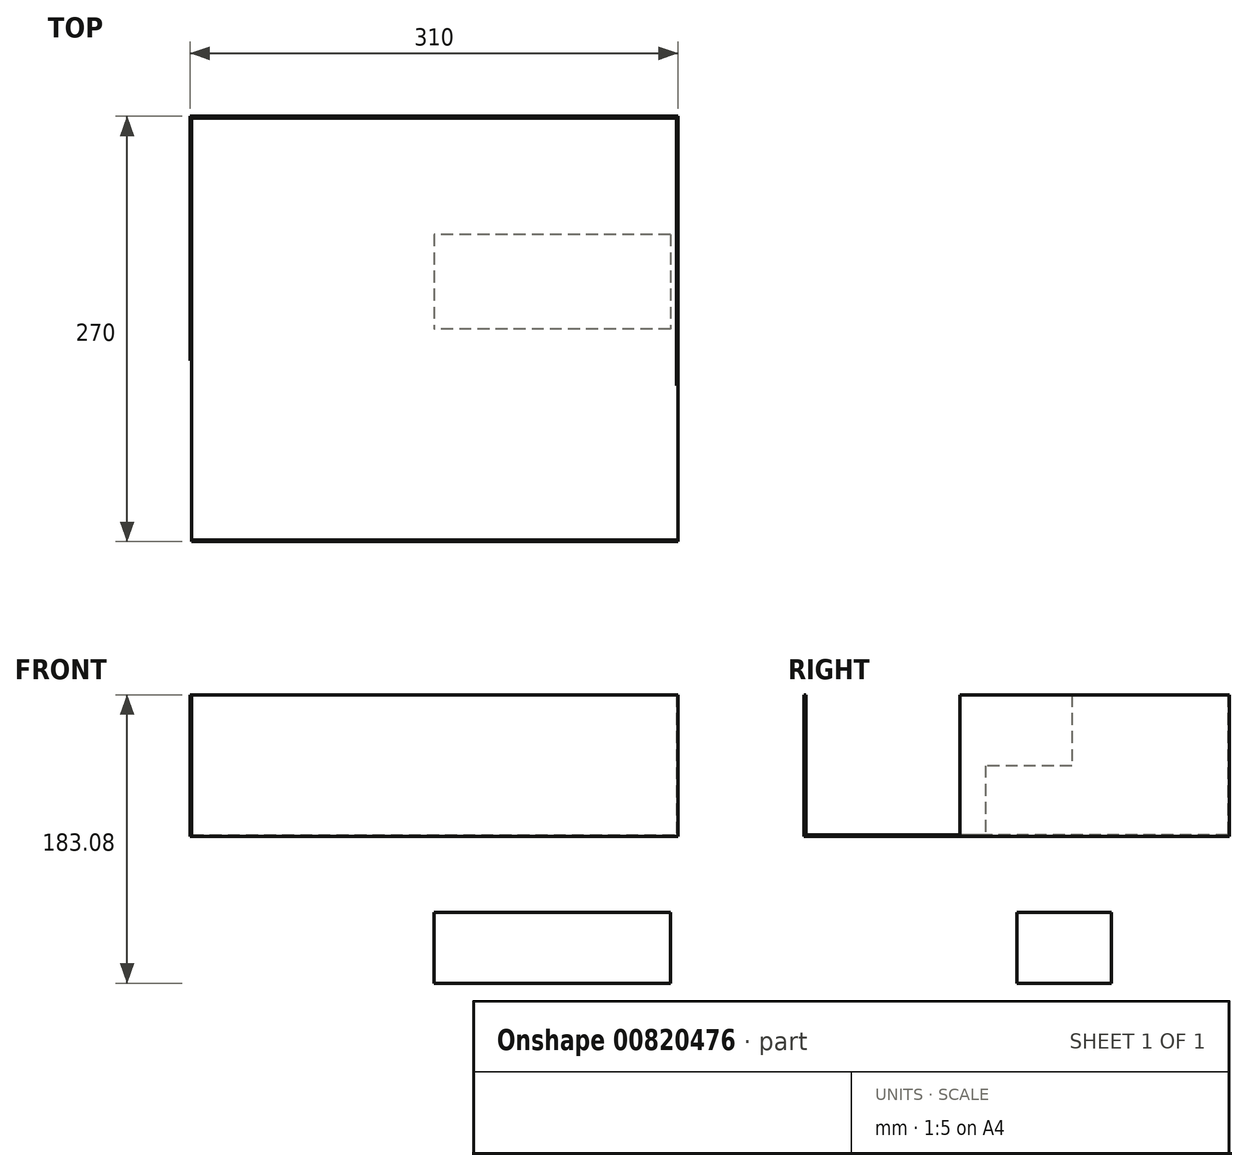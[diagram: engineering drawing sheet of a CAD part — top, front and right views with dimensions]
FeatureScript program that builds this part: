
annotation { "Feature Type Name" : "Feature", "Feature Type Description" : "" }
export const myFeature = defineFeature(function(context is Context, id is Id, definition is map)
    precondition{}
    {
        {
            var Q0;
            Q0=qCreatedBy(makeId("Top.planeOp"),FACE);
            var sketch = newSketch(context, id + "F0", { "sketchPlane" : qUnion([Q0])});
            skLineSegment(sketch, "E0.bottom", {"start": v(155, -135) * mm, "end": v(-155, -135) * mm});
            skLineSegment(sketch, "E0.top", {"start": v(155, 135) * mm, "end": v(-155, 135) * mm});
            skLineSegment(sketch, "E0.left", {"start": v(155, -135) * mm, "end": v(155, 135) * mm});
            skLineSegment(sketch, "E0.right", {"start": v(-155, -135) * mm, "end": v(-155, 135) * mm});
            skPoint(sketch, "E0.middle", {"position": v(0, 0) * mm});
            skLineSegment(sketch, "E1", {"start": v(-155, 135) * mm, "end": v(-155, 134) * mm});
            skLineSegment(sketch, "E2", {"start": v(-155, 134) * mm, "end": v(155, 134) * mm});
            skLineSegment(sketch, "E3", {"start": v(155, 134) * mm, "end": v(154, 134) * mm});
            skLineSegment(sketch, "E4", {"start": v(154, 134) * mm, "end": v(154, -36) * mm});
            skLineSegment(sketch, "E5", {"start": v(154, -36) * mm, "end": v(155, -36) * mm});
            skLineSegment(sketch, "E6", {"start": v(-155, 134) * mm, "end": v(-154, 134) * mm});
            skLineSegment(sketch, "E7", {"start": v(-154, 134) * mm, "end": v(-154, -135) * mm});
            skLineSegment(sketch, "E8", {"start": v(-154, -135) * mm, "end": v(-155, -135) * mm});
            skLineSegment(sketch, "E9", {"start": v(-154, -135) * mm, "end": v(-154, -134) * mm});
            skLineSegment(sketch, "E10", {"start": v(-154, -134) * mm, "end": v(155, -134) * mm});
            skLineSegment(sketch, "E11", {"start": v(155, -134) * mm, "end": v(155, -135) * mm});
            skLineSegment(sketch, "E12", {"start": v(-154, -135) * mm, "end": v(-154, -132.64) * mm});
            skLineSegment(sketch, "E13", {"start": v(-155, -135) * mm, "end": v(-155, 35) * mm});
            skLineSegment(sketch, "E14", {"start": v(-154, -135) * mm, "end": v(-154, 35) * mm});
            skLineSegment(sketch, "E15", {"start": v(-154, 35) * mm, "end": v(-155, 35) * mm});
            skLineSegment(sketch, "E16", {"start": v(-155, 35) * mm, "end": v(-155, -20) * mm});
            skLineSegment(sketch, "E17", {"start": v(-155, -20) * mm, "end": v(-154, -20) * mm});
            skLineSegment(sketch, "E18", {"start": v(-154, -20) * mm, "end": v(-154, 35) * mm});
            skSolve(sketch);
        }
        {
            var Q0;
            {var subQ6=sQuery(id+"F0.wireOp",EDGE,"E4");Q0=makeQuery(id+"F0.imprint","IMPRINT",FACE,{"disambiguationData":[TD([[makeQuery(id+"F0.imprint","IMPRINT",EDGE,{"derivedFrom":subQ6}),-1.0]])]});}
            extrude(context, id + "F1", {"entities" : qUnion([Q0]), "depth" : 1 * mm, "offsetDistance" : 25 * mm});
        }
        {
            var Q0;
            {var subQ4=sQuery(id+"F0.wireOp",EDGE,"E0.top");Q0=makeQuery(id+"F0.imprint","IMPRINT",FACE,{"disambiguationData":[TD([[makeQuery(id+"F0.imprint","IMPRINT",EDGE,{"derivedFrom":subQ4}),1.0]])]});}
            var Q1;
            {var subQ0=sQuery(id+"F0.wireOp",EDGE,"E15");Q1=makeQuery(id+"F0.imprint","IMPRINT",FACE,{"disambiguationData":[TD([[makeQuery(id+"F0.imprint","IMPRINT",EDGE,{"derivedFrom":subQ0}),-1.0]])]});}
            var Q2;
            {var subQ4=sQuery(id+"F0.wireOp",EDGE,"E4");Q2=makeQuery(id+"F0.imprint","IMPRINT",FACE,{"disambiguationData":[TD([[makeQuery(id+"F0.imprint","IMPRINT",EDGE,{"derivedFrom":subQ4}),1.0]])]});}
            var Q3;
            {var subQ5=sQuery(id+"F0.wireOp",EDGE,"E10");Q3=makeQuery(id+"F0.imprint","IMPRINT",FACE,{"disambiguationData":[TD([[makeQuery(id+"F0.imprint","IMPRINT",EDGE,{"derivedFrom":subQ5}),-1.0]])]});}
            extrude(context, id + "F2", {"entities" : qUnion([Q0, Q1, Q2, Q3]), "operationType" : NewBodyOperationType.ADD, "depth" : 90 * mm, "offsetDistance" : 25 * mm});
        }
        {
            var Q0;
            {var subQ0=sQuery(id+"F0.wireOp",EDGE,"E15");Q0=makeQuery(id+"F0.imprint","IMPRINT",FACE,{"disambiguationData":[TD([[makeQuery(id+"F0.imprint","IMPRINT",EDGE,{"derivedFrom":subQ0}),1.0]])]});}
            extrude(context, id + "F3", {"entities" : qUnion([Q0]), "operationType" : NewBodyOperationType.ADD, "depth" : 45 * mm, "offsetDistance" : 25 * mm});
        }
        {
            var Q0;
            Q0=qCreatedBy(makeId("Right.planeOp"),FACE);
            var sketch = newSketch(context, id + "F4", { "sketchPlane" : qUnion([Q0])});
            skLineSegment(sketch, "E19.bottom", {"start": v(60, -48.08) * mm, "end": v(0, -48.08) * mm});
            skLineSegment(sketch, "E19.top", {"start": v(60, -93.08) * mm, "end": v(0, -93.08) * mm});
            skLineSegment(sketch, "E19.left", {"start": v(60, -48.08) * mm, "end": v(60, -93.08) * mm});
            skLineSegment(sketch, "E19.right", {"start": v(0, -48.08) * mm, "end": v(0, -93.08) * mm});
            skSolve(sketch);
        }
        {
            var Q0;
            Q0=makeQuery(id+"F4.imprint","IMPRINT",FACE,{"disambiguationData":[TD([[makeQuery(id+"F4.imprint","IMPRINT",EDGE,{"derivedFrom":sQuery(id+"F4.wireOp",EDGE,"E19.bottom")}),1.0]])]});
            extrude(context, id + "F5", {"entities" : qUnion([Q0]), "depth" : 150 * mm, "offsetDistance" : 25 * mm});
        }
    });
